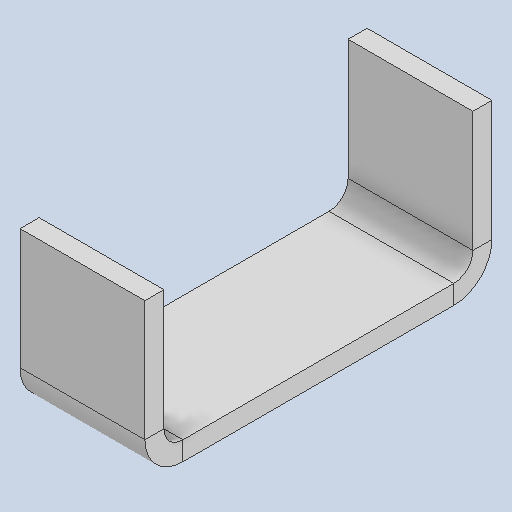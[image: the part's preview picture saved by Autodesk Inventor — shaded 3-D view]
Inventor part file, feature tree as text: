
AUTODESK INVENTOR PART (.ipt)
format: ipt  version: 2022 (Build 260153000, 153)  size: 129,024 bytes
history: native  units: in
note: dims shown in document units (in); Inventor stores cm internally (conversion verified against a paired STEP export)
features: sheet_metal_op x7, sketch x3, other x3
ambient origin geometry x8: Origin, YZ Plane, XZ Plane, XY Plane, X Axis, Y Axis, Z Axis, Center Point
bodies: Solid1 (feature_tree)
feature tree (13):
  sheet_metal_op  "Face1"
  sheet_metal_op  "Flange1"
  sheet_metal_op  "Flange2"
  sketch  "Sketch1"  dims[d0=2.189in]
  other  "Plate1"
  sketch  "Sketch2"  dims[d1=0.7874in]
  other  "Plate2"
  sheet_metal_op  "Bend1"
  sheet_metal_op  "Corner1"
  sketch  "Sketch3"  dims[d2=0.12in d3=0.12in d4=0.06in d5=0.24in d6=0.12in d7=1.0in d8=90.0deg d9=0.12in d10=0.48in d11=0.12in d12=0.12in d13=0.12in d14=0.06in d15=0.24in d16=0.12in d17=1.0in d18=90.0deg d19=0.12in d20=0.48in d21=0.12in d22=0.12in]
  other  "Plate3"
  sheet_metal_op  "Bend2"
  sheet_metal_op  "Corner2"
